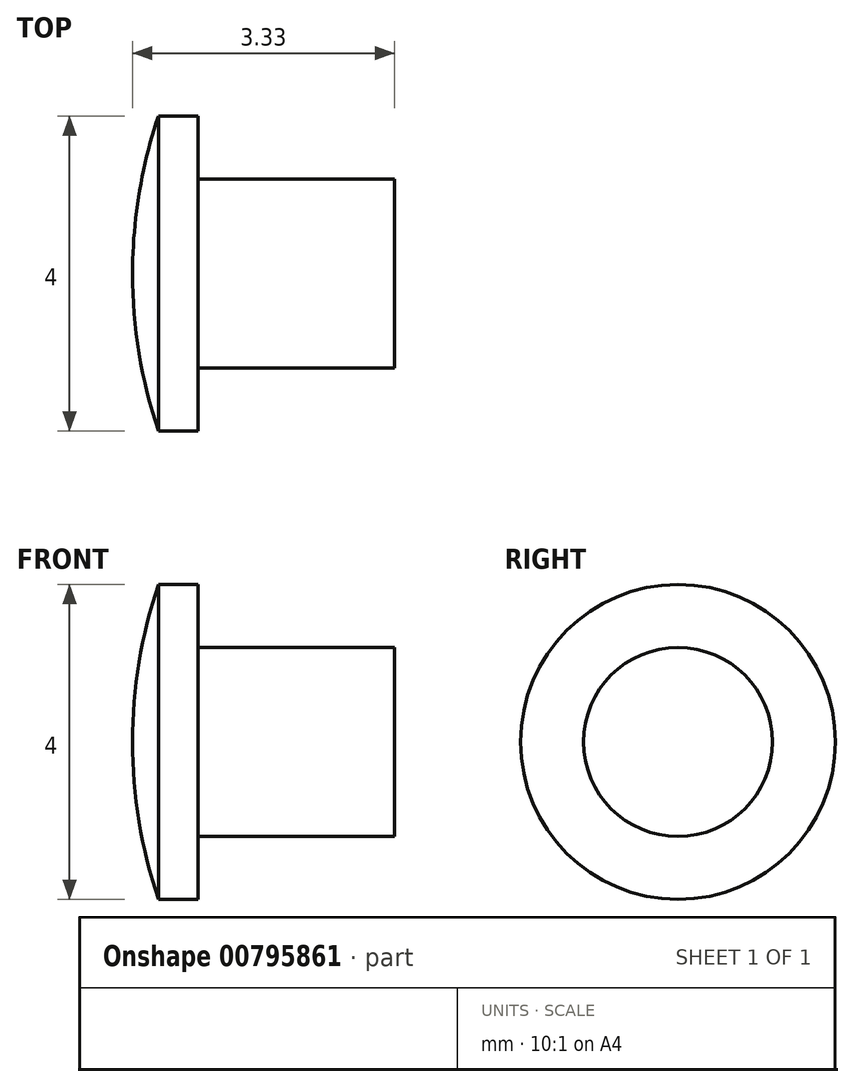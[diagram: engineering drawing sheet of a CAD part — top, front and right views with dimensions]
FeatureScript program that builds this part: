
annotation { "Feature Type Name" : "Feature", "Feature Type Description" : "" }
export const myFeature = defineFeature(function(context is Context, id is Id, definition is map)
    precondition{}
    {
        {
            var Q0;
            Q0=qCreatedBy(makeId("Top.planeOp"),FACE);
            var sketch = newSketch(context, id + "F0", { "sketchPlane" : qUnion([Q0])});
            skLineSegment(sketch, "E0", {"start": v(0, 1.2) * mm, "end": v(2.5, 1.2) * mm});
            skLineSegment(sketch, "E1", {"start": v(-0.5, 2) * mm, "end": v(0, 2) * mm});
            skLineSegment(sketch, "E2", {"start": v(0, 2) * mm, "end": v(0, 1.2) * mm});
            skLineSegment(sketch, "E3", {"start": v(-1.46, 0) * mm, "end": v(3.42, 0) * mm, "construction": true});
            skPoint(sketch, "E3.startSnap0", {"position": v(-0.83, 0) * mm});
            skLineSegment(sketch, "E4", {"start": v(2.5, 1.2) * mm, "end": v(2.5, 0) * mm});
            skArc(sketch, "E5", {"start": v(-0.83, 0) * mm, "mid": v(-0.75, 1.01) * mm, "end": v(-0.5, 2) * mm});
            skLineSegment(sketch, "E6", {"start": v(-0.83, 0) * mm, "end": v(2.5, 0) * mm});
            skSolve(sketch);
        }
        {
            var Q0;
            Q0 = qSketchRegion(id + "F0", true);
            var Q1;
            Q1=sQuery(id+"F0.wireOp",EDGE,"E3");
            revolve(context, id + "F1", {"surfaceOperationType" : NewSurfaceOperationType.NEW, "entities" : qUnion([Q0]), "axis" : qUnion([Q1]), "revolveType" : RevolveType.FULL});
        }
    });
